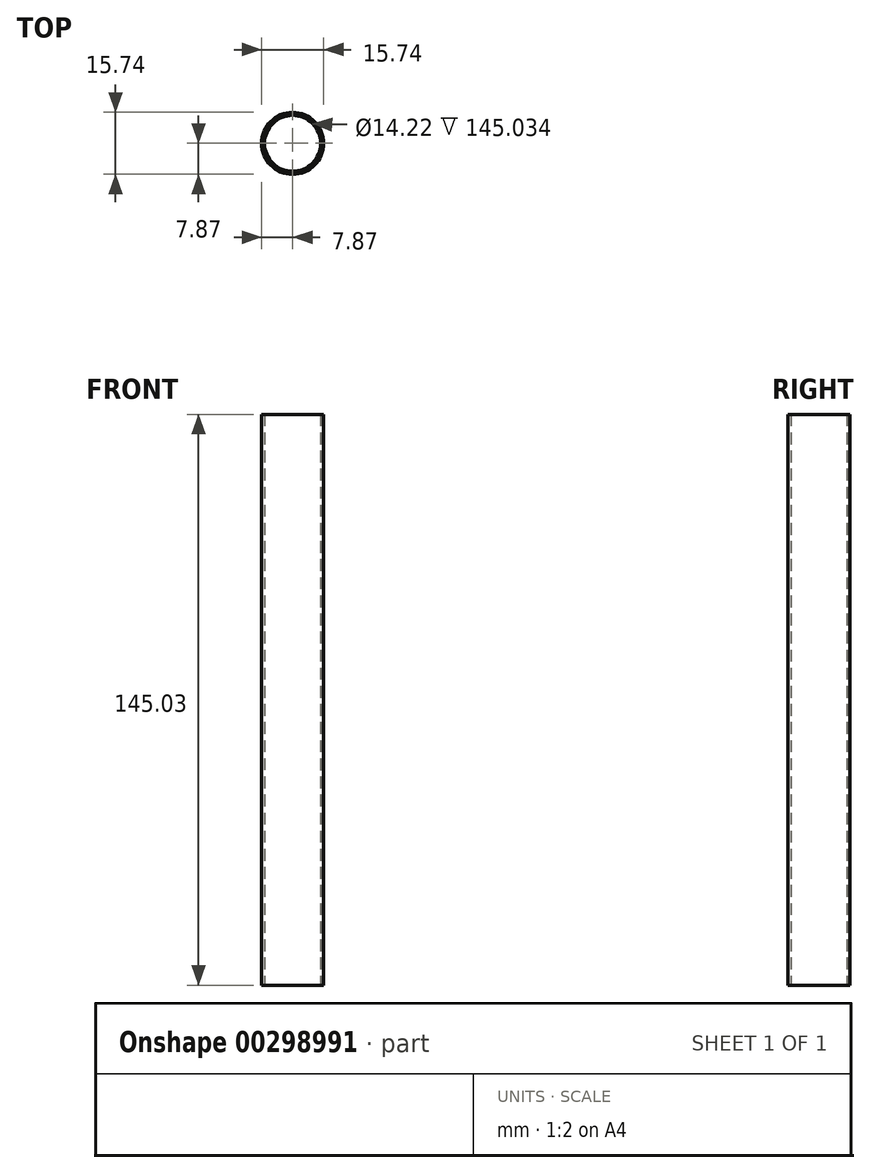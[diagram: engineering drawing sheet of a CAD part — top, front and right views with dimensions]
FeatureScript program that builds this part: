
annotation { "Feature Type Name" : "Feature", "Feature Type Description" : "" }
export const myFeature = defineFeature(function(context is Context, id is Id, definition is map)
    precondition{}
    {
        {
            var Q0;
            Q0=qCreatedBy(makeId("Top.planeOp"),FACE);
            var sketch = newSketch(context, id + "F0", { "sketchPlane" : qUnion([Q0])});
            skCircle(sketch, "E0", {"center": v(0, 0) * mm, "radius": 7.87 * mm});
            skCircle(sketch, "E1", {"center": v(0, 0) * mm, "radius": 7.11 * mm});
            skSolve(sketch);
        }
        {
            var Q0;
            Q0 = qSketchRegion(id + "F0", true);
            extrude(context, id + "F1", {"entities" : qUnion([Q0]), "depth" : 145.03 * mm});
        }
    });
